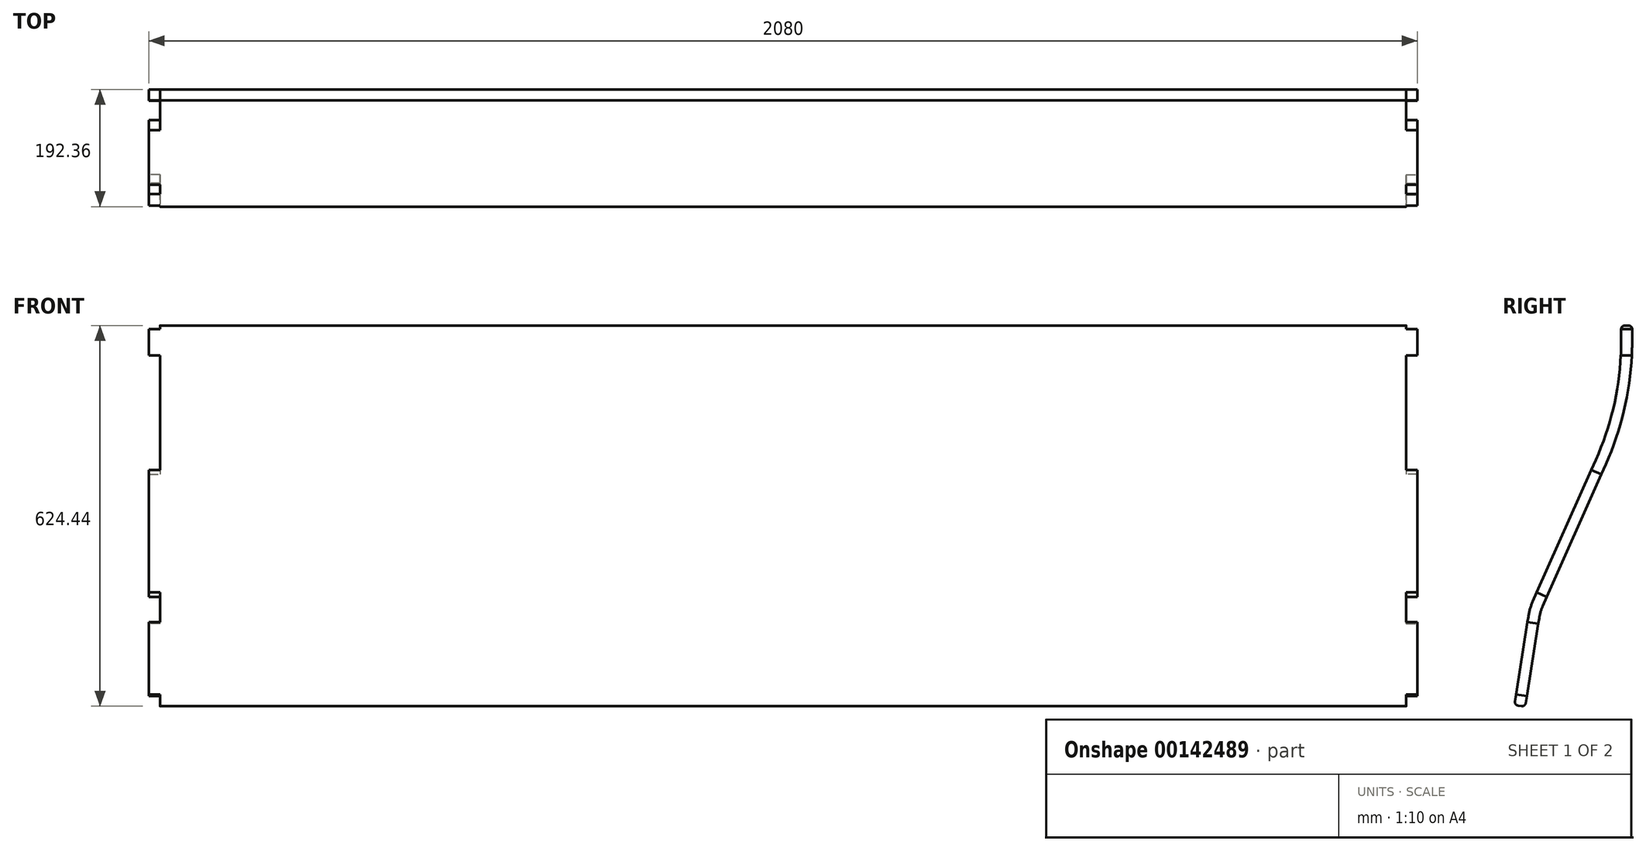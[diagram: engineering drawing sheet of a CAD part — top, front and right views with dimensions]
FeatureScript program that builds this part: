
annotation { "Feature Type Name" : "Feature", "Feature Type Description" : "" }
export const myFeature = defineFeature(function(context is Context, id is Id, definition is map)
    precondition{}
    {
        {
            var Q0;
            Q0=qCreatedBy(makeId("Right.planeOp"),FACE);
            var sketch = newSketch(context, id + "F0", { "sketchPlane" : qUnion([Q0])});
            skLineSegment(sketch, "E0", {"start": v(0.94, 5.93) * mm, "end": v(23, 145.2) * mm});
            skLineSegment(sketch, "E1", {"start": v(30.41, 170.22) * mm, "end": v(133.72, 402.26) * mm});
            skLineSegment(sketch, "E2", {"start": v(175.22, 597.5) * mm, "end": v(175.22, 616.5) * mm});
            skPoint(sketch, "E3.visualSharp", {"position": v(25.06, 158.2) * mm});
            skArc(sketch, "E3.filletArc", {"start": v(30.41, 170.22) * mm, "mid": v(25.88, 157.95) * mm, "end": v(23, 145.2) * mm});
            skPoint(sketch, "E4.visualSharp", {"position": v(175.22, 495.47) * mm});
            skArc(sketch, "E5.filletArc", {"start": v(133.72, 402.26) * mm, "mid": v(164.73, 497.7) * mm, "end": v(175.22, 597.5) * mm});
            skPoint(sketch, "E6.visualSharp", {"position": v(175.22, 639.68) * mm});
            skLineSegment(sketch, "E7.2", {"start": v(193.22, 597.5) * mm, "end": v(193.22, 616.5) * mm});
            skLineSegment(sketch, "E7.3", {"start": v(18.72, 3.11) * mm, "end": v(40.77, 142.37) * mm});
            skArc(sketch, "E7.4", {"start": v(46.85, 162.9) * mm, "mid": v(43.14, 152.84) * mm, "end": v(40.77, 142.37) * mm});
            skLineSegment(sketch, "E7.5", {"start": v(46.85, 162.9) * mm, "end": v(150.17, 394.94) * mm});
            skArc(sketch, "E7.6", {"start": v(150.17, 394.94) * mm, "mid": v(182.34, 493.95) * mm, "end": v(193.22, 597.5) * mm});
            skLineSegment(sketch, "E8", {"start": v(11.85, -1.88) * mm, "end": v(5.93, -0.94) * mm});
            skPoint(sketch, "E9.visualSharp", {"position": v(0, 0) * mm});
            skArc(sketch, "E9.filletArc", {"start": v(0.94, 5.93) * mm, "mid": v(2.01, 1.46) * mm, "end": v(5.93, -0.94) * mm});
            skPoint(sketch, "E10.visualSharp", {"position": v(17.78, -2.82) * mm});
            skArc(sketch, "E10.filletArc", {"start": v(11.85, -1.88) * mm, "mid": v(16.32, -0.8) * mm, "end": v(18.72, 3.11) * mm});
            skPoint(sketch, "E11.visualSharp", {"position": v(165.74, 677.71) * mm});
            skPoint(sketch, "E12.visualSharp", {"position": v(183.2, 682.06) * mm});
            skLineSegment(sketch, "E13", {"start": v(181.22, 622.5) * mm, "end": v(187.22, 622.5) * mm});
            skPoint(sketch, "E14.visualSharp", {"position": v(175.22, 622.5) * mm});
            skArc(sketch, "E14.filletArc", {"start": v(181.22, 622.5) * mm, "mid": v(176.98, 620.74) * mm, "end": v(175.22, 616.5) * mm});
            skPoint(sketch, "E15.visualSharp", {"position": v(193.22, 622.5) * mm});
            skArc(sketch, "E15.filletArc", {"start": v(193.22, 616.5) * mm, "mid": v(191.46, 620.74) * mm, "end": v(187.22, 622.5) * mm});
            skSolve(sketch);
        }
        {
            var Q0;
            Q0 = qSketchRegion(id + "F0", true);
            extrude(context, id + "F1", {"entities" : qUnion([Q0]), "depth" : 2080 * mm});
        }
        {
            var Q0;
            Q0=makeQuery(id+"F1.opExtrude","SWEPT_FACE",FACE,{"disambiguationData":[OSD([sQuery(id+"F0.wireOp",EDGE,"E0")])]});
            var sketch = newSketch(context, id + "F2", { "sketchPlane" : qUnion([Q0])});
            skLineSegment(sketch, "E16.0", {"start": v(18, -25.72) * mm, "end": v(18, 17.77) * mm});
            skLineSegment(sketch, "E17", {"start": v(-14.76, 164.26) * mm, "end": v(-14.76, 137.77) * mm});
            skLineSegment(sketch, "E18", {"start": v(18, 164.26) * mm, "end": v(-14.76, 164.26) * mm});
            skLineSegment(sketch, "E19", {"start": v(18, -25.72) * mm, "end": v(-14.76, -25.72) * mm});
            skLineSegment(sketch, "E20", {"start": v(18, 17.77) * mm, "end": v(-14.76, 17.77) * mm});
            skLineSegment(sketch, "E21", {"start": v(18, 137.77) * mm, "end": v(-14.76, 137.77) * mm});
            skLineSegment(sketch, "E22", {"start": v(1040, 6) * mm, "end": v(1040, 686.3) * mm, "construction": true});
            skLineSegment(sketch, "E23.trimOffspring", {"start": v(-14.76, 17.77) * mm, "end": v(-14.76, -25.72) * mm});
            skLineSegment(sketch, "E24.trimOffspring", {"start": v(18, 137.77) * mm, "end": v(18, 164.26) * mm});
            skPoint(sketch, "E25.orphan", {"position": v(-42.22, 17.77) * mm});
            skPoint(sketch, "E26.orphan", {"position": v(-42.22, -25.72) * mm});
            skLineSegment(sketch, "E27.MirrorCS", {"start": v(2062, 137.77) * mm, "end": v(2062, 164.26) * mm});
            skLineSegment(sketch, "E28.MirrorCS", {"start": v(2062, -25.72) * mm, "end": v(2094.76, -25.72) * mm});
            skLineSegment(sketch, "E29.MirrorCS", {"start": v(2094.76, 164.26) * mm, "end": v(2094.76, 137.77) * mm});
            skLineSegment(sketch, "E30.MirrorCS", {"start": v(2094.76, 17.77) * mm, "end": v(2094.76, -25.72) * mm});
            skLineSegment(sketch, "E31.MirrorCS", {"start": v(2062, 17.77) * mm, "end": v(2094.76, 17.77) * mm});
            skLineSegment(sketch, "E32.MirrorCS", {"start": v(2062, 164.26) * mm, "end": v(2094.76, 164.26) * mm});
            skLineSegment(sketch, "E33.MirrorCS", {"start": v(2062, -25.72) * mm, "end": v(2062, 17.77) * mm});
            skLineSegment(sketch, "E34.MirrorCS", {"start": v(2062, 137.77) * mm, "end": v(2094.76, 137.77) * mm});
            skPoint(sketch, "E35.MirrorP", {"position": v(2122.22, -25.72) * mm});
            skPoint(sketch, "E36.MirrorP", {"position": v(2122.22, 17.77) * mm});
            skSolve(sketch);
        }
        {
            var Q0;
            Q0 = qSketchRegion(id + "F2", true);
            extrude(context, id + "F3", {"entities" : qUnion([Q0]), "operationType" : NewBodyOperationType.REMOVE, "oppositeDirection" : true, "depth" : 25 * mm});
        }
        {
            var Q0;
            Q0=makeQuery(id+"F1.opExtrude","SWEPT_FACE",FACE,{"disambiguationData":[OSD([sQuery(id+"F0.wireOp",EDGE,"E1")])]});
            var sketch = newSketch(context, id + "F4", { "sketchPlane" : qUnion([Q0])});
            skLineSegment(sketch, "E37.0", {"start": v(18, 149.12) * mm, "end": v(18, 183.73) * mm});
            skLineSegment(sketch, "E38", {"start": v(18, 403.73) * mm, "end": v(-26.81, 403.73) * mm});
            skLineSegment(sketch, "E39", {"start": v(-26.81, 183.73) * mm, "end": v(18, 183.73) * mm});
            skLineSegment(sketch, "E40", {"start": v(18, 149.12) * mm, "end": v(-26.81, 149.12) * mm});
            skLineSegment(sketch, "E41", {"start": v(18, 591.4) * mm, "end": v(-26.81, 591.4) * mm});
            skLineSegment(sketch, "E42", {"start": v(-26.81, 591.4) * mm, "end": v(-26.81, 403.73) * mm});
            skLineSegment(sketch, "E43.trimOffspring", {"start": v(18, 403.73) * mm, "end": v(18, 591.4) * mm});
            skLineSegment(sketch, "E44.trimOffspring", {"start": v(-26.81, 183.73) * mm, "end": v(-26.81, 149.12) * mm});
            skLineSegment(sketch, "E45", {"start": v(1040, 167.87) * mm, "end": v(1040, 806.27) * mm, "construction": true});
            skLineSegment(sketch, "E46.MirrorCS", {"start": v(2062, 591.4) * mm, "end": v(2106.81, 591.4) * mm});
            skLineSegment(sketch, "E47.MirrorCS", {"start": v(2062, 149.12) * mm, "end": v(2106.81, 149.12) * mm});
            skLineSegment(sketch, "E48.MirrorCS", {"start": v(2106.81, 183.73) * mm, "end": v(2106.81, 149.12) * mm});
            skLineSegment(sketch, "E49.MirrorCS", {"start": v(2106.81, 183.73) * mm, "end": v(2062, 183.73) * mm});
            skLineSegment(sketch, "E50.MirrorCS", {"start": v(2062, 403.73) * mm, "end": v(2106.81, 403.73) * mm});
            skLineSegment(sketch, "E51.MirrorCS", {"start": v(2062, 149.12) * mm, "end": v(2062, 183.73) * mm});
            skLineSegment(sketch, "E52.MirrorCS", {"start": v(2062, 403.73) * mm, "end": v(2062, 591.4) * mm});
            skLineSegment(sketch, "E53.MirrorCS", {"start": v(2106.81, 591.4) * mm, "end": v(2106.81, 403.73) * mm});
            skSolve(sketch);
        }
        {
            var Q0;
            Q0 = qSketchRegion(id + "F4", true);
            extrude(context, id + "F5", {"entities" : qUnion([Q0]), "operationType" : NewBodyOperationType.REMOVE, "depth" : 88.72 * mm, "hasSecondDirection" : true, "secondDirectionOppositeDirection" : true, "secondDirectionDepth" : 90.01 * mm});
        }
        {
            var Q0;
            Q0=makeQuery(id+"F1.opExtrude","SWEPT_FACE",FACE,{"disambiguationData":[OSD([sQuery(id+"F0.wireOp",EDGE,"E2")])]});
            var sketch = newSketch(context, id + "F6", { "sketchPlane" : qUnion([Q0])});
            skLineSegment(sketch, "E54.0", {"start": v(18, 550.85) * mm, "end": v(18, 573.56) * mm});
            skLineSegment(sketch, "E55", {"start": v(-9.19, 616.5) * mm, "end": v(18, 616.5) * mm});
            skLineSegment(sketch, "E56", {"start": v(-9.19, 573.56) * mm, "end": v(18, 573.56) * mm});
            skLineSegment(sketch, "E57", {"start": v(-9.19, 550.85) * mm, "end": v(-9.19, 573.56) * mm});
            skLineSegment(sketch, "E58", {"start": v(18, 636.69) * mm, "end": v(-9.19, 636.69) * mm});
            skLineSegment(sketch, "E59", {"start": v(18, 550.85) * mm, "end": v(-9.19, 550.85) * mm});
            skLineSegment(sketch, "E60.trimOffspring", {"start": v(18, 616.5) * mm, "end": v(18, 636.69) * mm});
            skLineSegment(sketch, "E61.trimOffspring", {"start": v(-9.19, 616.5) * mm, "end": v(-9.19, 636.69) * mm});
            skLineSegment(sketch, "E62", {"start": v(1040, 597.5) * mm, "end": v(1040, 939.14) * mm, "construction": true});
            skLineSegment(sketch, "E63.MirrorCS", {"start": v(2062, 550.85) * mm, "end": v(2089.19, 550.85) * mm});
            skLineSegment(sketch, "E64.MirrorCS", {"start": v(2062, 636.69) * mm, "end": v(2089.19, 636.69) * mm});
            skLineSegment(sketch, "E65.MirrorCS", {"start": v(2089.19, 550.85) * mm, "end": v(2089.19, 573.56) * mm});
            skLineSegment(sketch, "E66.MirrorCS", {"start": v(2062, 616.5) * mm, "end": v(2062, 636.69) * mm});
            skLineSegment(sketch, "E67.MirrorCS", {"start": v(2089.19, 573.56) * mm, "end": v(2062, 573.56) * mm});
            skLineSegment(sketch, "E68.MirrorCS", {"start": v(2089.19, 616.5) * mm, "end": v(2089.19, 636.69) * mm});
            skLineSegment(sketch, "E69.MirrorCS", {"start": v(2062, 550.85) * mm, "end": v(2062, 573.56) * mm});
            skLineSegment(sketch, "E70.MirrorCS", {"start": v(2089.19, 616.5) * mm, "end": v(2062, 616.5) * mm});
            skSolve(sketch);
        }
        {
            var Q0;
            Q0 = qSketchRegion(id + "F6", true);
            extrude(context, id + "F7", {"entities" : qUnion([Q0]), "operationType" : NewBodyOperationType.REMOVE, "oppositeDirection" : true, "depth" : 25 * mm});
        }
        {
            var Q0;
            Q0 = qSketchRegion(id + "F6", true);
            extrude(context, id + "F8", {"entities" : qUnion([Q0]), "operationType" : NewBodyOperationType.REMOVE, "depth" : 29.82 * mm});
        }
    });
